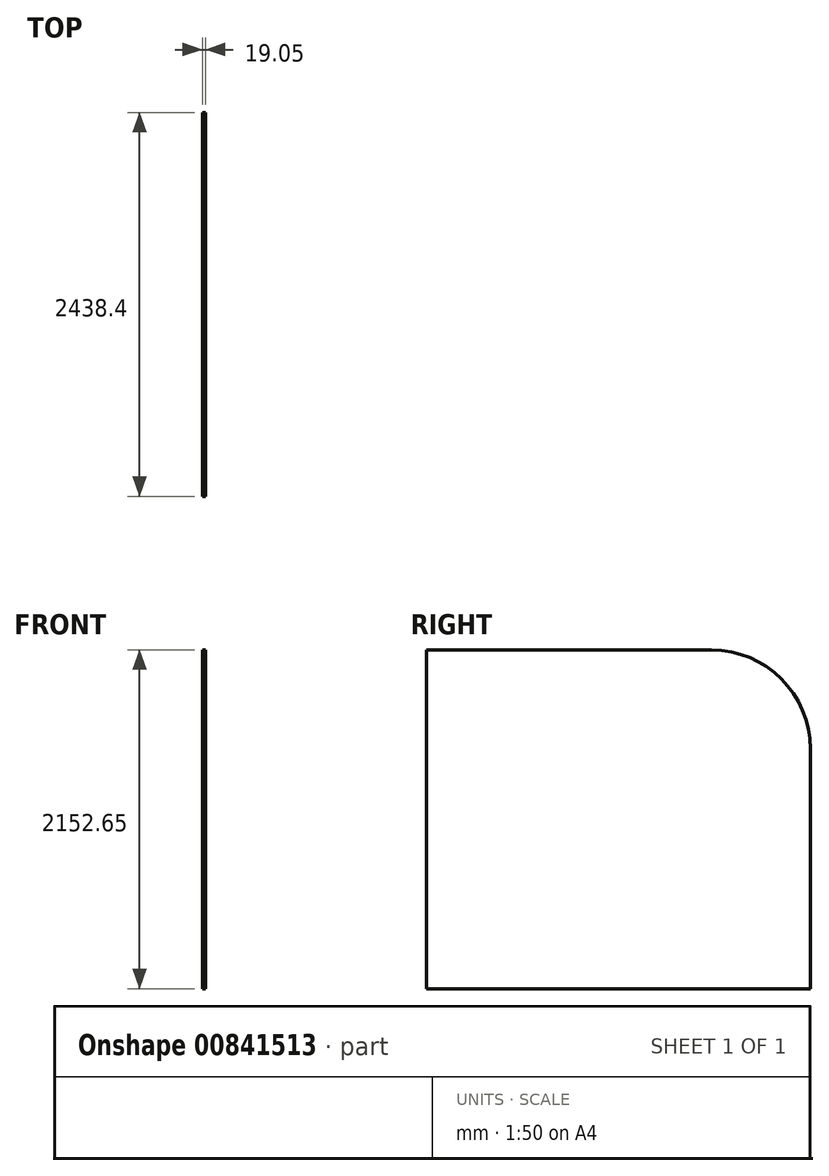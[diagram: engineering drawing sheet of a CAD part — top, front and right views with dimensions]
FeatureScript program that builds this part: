
annotation { "Feature Type Name" : "Feature", "Feature Type Description" : "" }
export const myFeature = defineFeature(function(context is Context, id is Id, definition is map)
    precondition{}
    {
        {
            var Q0;
            Q0=qCreatedBy(makeId("Right.planeOp"),FACE);
            var sketch = newSketch(context, id + "F0", { "sketchPlane" : qUnion([Q0])});
            skLineSegment(sketch, "E0.bottom", {"start": v(0, 0) * mm, "end": v(-1524, 0) * mm});
            skLineSegment(sketch, "E0.top", {"start": v(0, 2152.65) * mm, "end": v(-1524, 2152.65) * mm});
            skLineSegment(sketch, "E0.left", {"start": v(0, 0) * mm, "end": v(0, 2152.65) * mm});
            skLineSegment(sketch, "E0.right", {"start": v(-1524, 0) * mm, "end": v(-1524, 2152.65) * mm});
            skSolve(sketch);
        }
        {
            var Q0;
            Q0=qSketchRegion(id+"F0",true);
            extrude(context, id + "F1", {"entities" : qUnion([Q0]), "depth" : 19.05 * mm, "offsetDistance" : 25.4 * mm});
        }
        {
            var Q0;
            Q0=qCreatedBy(makeId("Right.planeOp"),FACE);
            var sketch = newSketch(context, id + "F2", { "sketchPlane" : qUnion([Q0])});
            skLineSegment(sketch, "E1.bottom", {"start": v(-1524, 0) * mm, "end": v(-2438.4, 0) * mm});
            skLineSegment(sketch, "E1.top", {"start": v(-1524, 2152.65) * mm, "end": v(-2438.4, 2152.65) * mm});
            skLineSegment(sketch, "E1.left", {"start": v(-1524, 0) * mm, "end": v(-1524, 2152.65) * mm});
            skLineSegment(sketch, "E1.right", {"start": v(-2438.4, 0) * mm, "end": v(-2438.4, 2152.65) * mm});
            skSolve(sketch);
        }
        {
            var Q0;
            Q0=makeQuery(id+"F2.imprint","IMPRINT",FACE,{"disambiguationData":[TD([[makeQuery(id+"F2.imprint","IMPRINT",EDGE,{"derivedFrom":sQuery(id+"F2.wireOp",EDGE,"E1.bottom")}),-1.0]])]});
            extrude(context, id + "F3", {"entities" : qUnion([Q0]), "operationType" : NewBodyOperationType.ADD, "depth" : 19.05 * mm, "offsetDistance" : 25.4 * mm});
        }
        {
            var Q0;
            Q0=makeQuery(id+"F3.boolean.opBoolean","MERGE",FACE,{"derivedFrom":[makeQuery(id+"F1.opExtrude","CAP_FACE",FACE,{"disambiguationData":[OSD([sQuery(id+"F0.wireOp",EDGE,"E0.bottom"),sQuery(id+"F0.wireOp",EDGE,"E0.top"),sQuery(id+"F0.wireOp",EDGE,"E0.left"),sQuery(id+"F0.wireOp",EDGE,"E0.right")])],"isStart":false}),makeQuery(id+"F3.opExtrude","CAP_FACE",FACE,{"disambiguationData":[OSD([sQuery(id+"F2.wireOp",EDGE,"E1.bottom"),sQuery(id+"F2.wireOp",EDGE,"E1.top"),sQuery(id+"F2.wireOp",EDGE,"E1.left"),sQuery(id+"F2.wireOp",EDGE,"E1.right")])],"isStart":false})]});
            var sketch = newSketch(context, id + "F4", { "sketchPlane" : qUnion([Q0])});
            skArc(sketch, "E2", {"start": v(0, 1524) * mm, "mid": v(-184.13, 1968.52) * mm, "end": v(-628.65, 2152.65) * mm});
            skLineSegment(sketch, "E3", {"start": v(-628.65, 2152.65) * mm, "end": v(0, 2152.65) * mm});
            skLineSegment(sketch, "E4", {"start": v(0, 2152.65) * mm, "end": v(0, 1524) * mm});
            skSolve(sketch);
        }
        {
            var Q0;
            Q0=qSketchRegion(id+"F4",true);
            extrude(context, id + "F5", {"entities" : qUnion([Q0]), "operationType" : NewBodyOperationType.REMOVE, "oppositeDirection" : true, "depth" : 25.4 * mm, "offsetDistance" : 25.4 * mm});
        }
    });
